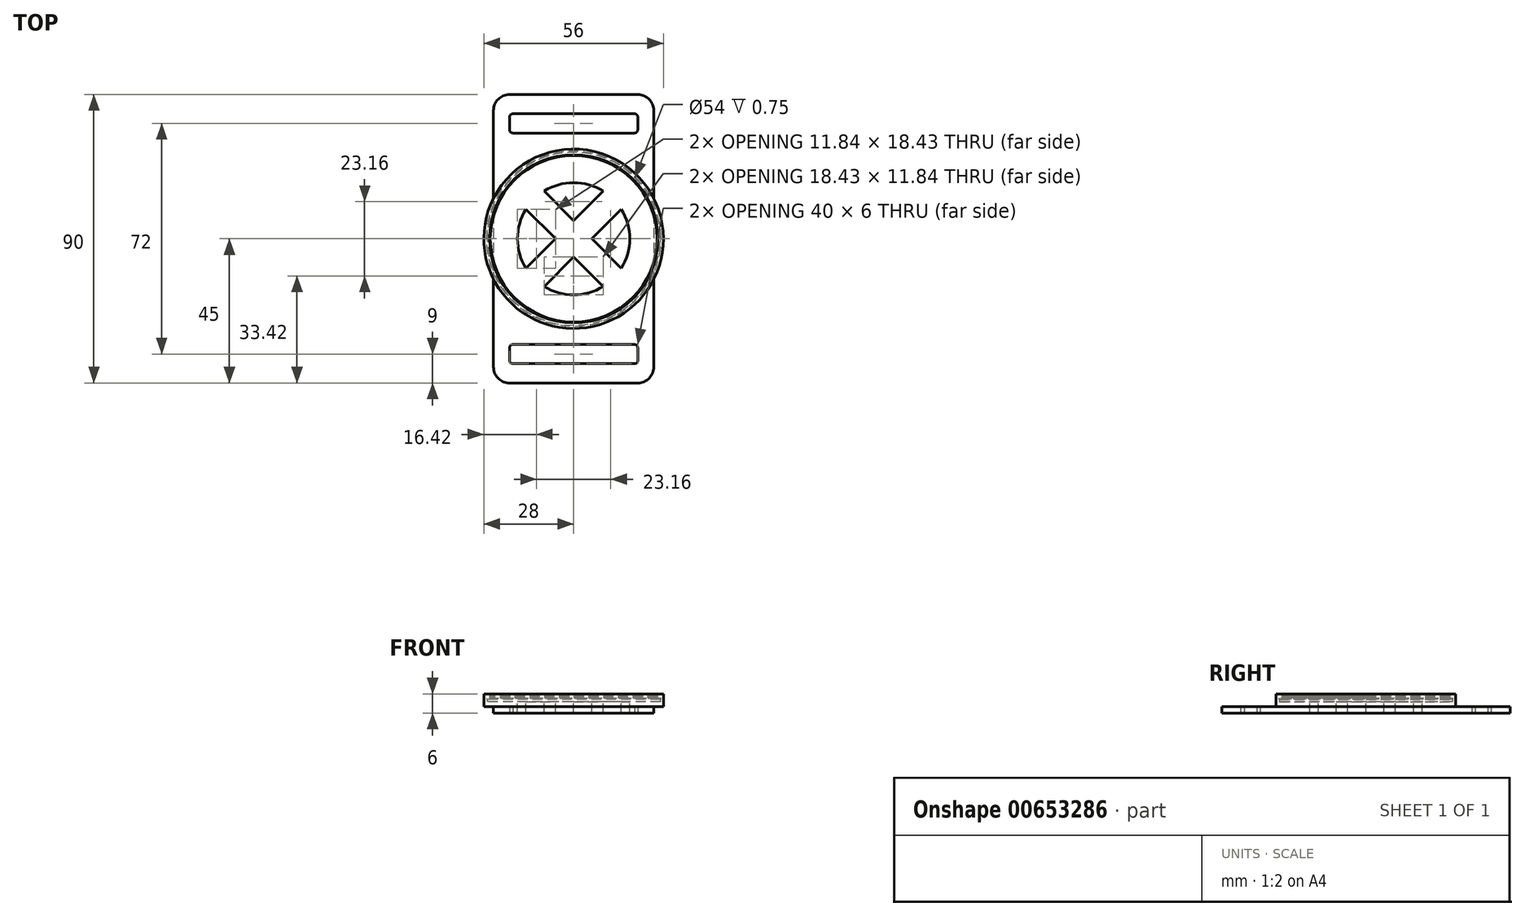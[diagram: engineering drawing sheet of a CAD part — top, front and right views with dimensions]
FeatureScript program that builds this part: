
annotation { "Feature Type Name" : "Feature", "Feature Type Description" : "" }
export const myFeature = defineFeature(function(context is Context, id is Id, definition is map)
    precondition{}
    {
        {
            var Q0;
            Q0=qCreatedBy(makeId("Top.planeOp"),FACE);
            var sketch = newSketch(context, id + "F0", { "sketchPlane" : qUnion([Q0])});
            skLineSegment(sketch, "E0.bottom", {"start": v(-25, 45) * mm, "end": v(25, 45) * mm});
            skLineSegment(sketch, "E0.top", {"start": v(-25, -45) * mm, "end": v(25, -45) * mm});
            skLineSegment(sketch, "E0.left", {"start": v(-25, 45) * mm, "end": v(-25, -45) * mm});
            skLineSegment(sketch, "E0.right", {"start": v(25, 45) * mm, "end": v(25, -45) * mm});
            skLineSegment(sketch, "E1", {"start": v(-25, 0) * mm, "end": v(25, 0) * mm, "construction": true});
            skLineSegment(sketch, "E2", {"start": v(0, -45) * mm, "end": v(0, 45) * mm, "construction": true});
            skPoint(sketch, "E3", {"position": v(0, 0) * mm});
            skSolve(sketch);
        }
        {
            var Q0;
            Q0 = qSketchRegion(id + "F0", true);
            extrude(context, id + "F1", {"entities" : qUnion([Q0]), "depth" : 2 * mm, "offsetDistance" : 25 * mm});
        }
        {
            var Q0;
            Q0=makeQuery(id+"F1.opExtrude","CAP_FACE",FACE,{"disambiguationData":[OSD([sQuery(id+"F0.wireOp",EDGE,"E0.bottom"),sQuery(id+"F0.wireOp",EDGE,"E0.top"),sQuery(id+"F0.wireOp",EDGE,"E0.left"),sQuery(id+"F0.wireOp",EDGE,"E0.right")])],"isStart":false});
            var sketch = newSketch(context, id + "F2", { "sketchPlane" : qUnion([Q0])});
            skCircle(sketch, "E4", {"center": v(0, 0) * mm, "radius": 28 * mm});
            skSolve(sketch);
        }
        {
            var Q0;
            Q0 = qSketchRegion(id + "F2", true);
            extrude(context, id + "F3", {"entities" : qUnion([Q0]), "operationType" : NewBodyOperationType.ADD, "depth" : 1.5 * mm, "offsetDistance" : 25 * mm});
        }
        {
            var Q0;
            Q0=makeQuery(id+"F3.opExtrude","CAP_FACE",FACE,{"disambiguationData":[OSD([sQuery(id+"F2.wireOp",EDGE,"E4")])],"isStart":false});
            var sketch = newSketch(context, id + "F4", { "sketchPlane" : qUnion([Q0])});
            skCircle(sketch, "E5", {"center": v(0, 0) * mm, "radius": 27 * mm});
            skSolve(sketch);
        }
        {
            var Q0;
            Q0=makeQuery(id+"F4.imprint","IMPRINT",FACE,{"disambiguationData":[TD([[makeQuery(id+"F4.imprint","IMPRINT",EDGE,{"derivedFrom":sQuery(id+"F4.wireOp",EDGE,"E5")}),-1.0]])]});
            extrude(context, id + "F5", {"entities" : qUnion([Q0]), "operationType" : NewBodyOperationType.ADD, "depth" : 1 * mm, "offsetDistance" : 25 * mm});
        }
        {
            var Q0;
            Q0=makeQuery(id+"F1.opExtrude","CAP_FACE",FACE,{"disambiguationData":[OSD([sQuery(id+"F0.wireOp",EDGE,"E0.bottom"),sQuery(id+"F0.wireOp",EDGE,"E0.top"),sQuery(id+"F0.wireOp",EDGE,"E0.left"),sQuery(id+"F0.wireOp",EDGE,"E0.right")])],"isStart":true});
            var sketch = newSketch(context, id + "F6", { "sketchPlane" : qUnion([Q0])});
            skLineSegment(sketch, "E6.bottom", {"start": v(-25, 35) * mm, "end": v(-22, 35) * mm});
            skLineSegment(sketch, "E6.top", {"start": v(-25, -35) * mm, "end": v(-22, -35) * mm});
            skLineSegment(sketch, "E6.left", {"start": v(-25, 35) * mm, "end": v(-25, -35) * mm});
            skLineSegment(sketch, "E6.right", {"start": v(-22, 35) * mm, "end": v(-22, -35) * mm});
            skLineSegment(sketch, "E7.bottom", {"start": v(22, 35) * mm, "end": v(25, 35) * mm});
            skLineSegment(sketch, "E7.top", {"start": v(22, -35) * mm, "end": v(25, -35) * mm});
            skLineSegment(sketch, "E7.left", {"start": v(22, 35) * mm, "end": v(22, -35) * mm});
            skLineSegment(sketch, "E7.right", {"start": v(25, 35) * mm, "end": v(25, -35) * mm});
            skSolve(sketch);
        }
        {
            var Q0;
            Q0=makeQuery(id+"F6.imprint","IMPRINT",FACE,{"disambiguationData":[TD([[makeQuery(id+"F6.imprint","IMPRINT",EDGE,{"derivedFrom":sQuery(id+"F6.wireOp",EDGE,"E6.bottom")}),-1.0]])]});
            var Q1;
            Q1=makeQuery(id+"F6.imprint","IMPRINT",FACE,{"disambiguationData":[TD([[makeQuery(id+"F6.imprint","IMPRINT",EDGE,{"derivedFrom":sQuery(id+"F6.wireOp",EDGE,"E7.bottom")}),-1.0]])]});
            extrude(context, id + "F7", {"entities" : qUnion([Q0, Q1]), "operationType" : NewBodyOperationType.ADD, "depth" : 3 * mm, "offsetDistance" : 25 * mm});
        }
        {
            var Q0;
            {var subQ0=sQuery(id+"F6.wireOp",EDGE,"E6.right");var subQ2=sQuery(id+"F6.wireOp",EDGE,"E6.left");var subQ3=sQuery(id+"F6.wireOp",EDGE,"E6.top");Q0=makeQuery(id+"Fcp3DyhTEGZhcjd_1.boolean.opBoolean","SPLIT",FACE,{"disambiguationData":[TD([makeQuery(id+"F7.opExtrude","SWEPT_FACE",FACE,{"disambiguationData":[OSD([subQ3])]})])],"derivedFrom":makeQuery(id+"F7.opExtrude","CAP_FACE",FACE,{"disambiguationData":[OSD([sQuery(id+"F6.wireOp",EDGE,"E6.bottom"),subQ3,subQ2,subQ0])],"isStart":false})});}
            var Q1;
            {var subQ0=sQuery(id+"F6.wireOp",EDGE,"E7.right");var subQ1=sQuery(id+"F6.wireOp",EDGE,"E7.left");var subQ2=sQuery(id+"F6.wireOp",EDGE,"E7.top");Q1=makeQuery(id+"Fcp3DyhTEGZhcjd_1.boolean.opBoolean","SPLIT",FACE,{"disambiguationData":[TD([makeQuery(id+"F7.opExtrude","SWEPT_FACE",FACE,{"disambiguationData":[OSD([subQ2])]})])],"derivedFrom":makeQuery(id+"F7.opExtrude","CAP_FACE",FACE,{"disambiguationData":[OSD([sQuery(id+"F6.wireOp",EDGE,"E7.bottom"),subQ2,subQ1,subQ0])],"isStart":false})});}
            var Q2;
            {var subQ0=sQuery(id+"F6.wireOp",EDGE,"E6.left");var subQ1=sQuery(id+"F6.wireOp",EDGE,"E6.right");var subQ3=sQuery(id+"F6.wireOp",EDGE,"E6.bottom");Q2=makeQuery(id+"Fcp3DyhTEGZhcjd_1.boolean.opBoolean","SPLIT",FACE,{"disambiguationData":[TD([makeQuery(id+"F7.opExtrude","SWEPT_FACE",FACE,{"disambiguationData":[OSD([subQ3])]})])],"derivedFrom":makeQuery(id+"F7.opExtrude","CAP_FACE",FACE,{"disambiguationData":[OSD([subQ3,sQuery(id+"F6.wireOp",EDGE,"E6.top"),subQ0,subQ1])],"isStart":false})});}
            var Q3;
            {var subQ0=sQuery(id+"F6.wireOp",EDGE,"E7.left");var subQ1=sQuery(id+"F6.wireOp",EDGE,"E7.right");var subQ2=sQuery(id+"F6.wireOp",EDGE,"E7.bottom");Q3=makeQuery(id+"Fcp3DyhTEGZhcjd_1.boolean.opBoolean","SPLIT",FACE,{"disambiguationData":[TD([makeQuery(id+"F7.opExtrude","SWEPT_FACE",FACE,{"disambiguationData":[OSD([subQ2])]})])],"derivedFrom":makeQuery(id+"F7.opExtrude","CAP_FACE",FACE,{"disambiguationData":[OSD([subQ2,sQuery(id+"F6.wireOp",EDGE,"E7.top"),subQ0,subQ1])],"isStart":false})});}
            var Q4;
            Q4=makeQuery(id+"F1.opExtrude","CAP_FACE",FACE,{"disambiguationData":[OSD([sQuery(id+"F0.wireOp",EDGE,"E0.bottom"),sQuery(id+"F0.wireOp",EDGE,"E0.top"),sQuery(id+"F0.wireOp",EDGE,"E0.left"),sQuery(id+"F0.wireOp",EDGE,"E0.right")])],"isStart":true});
            extrude(context, id + "F8", {"entities" : qUnion([Q0, Q1, Q2, Q3]), "operationType" : NewBodyOperationType.REMOVE, "endBound" : BoundingType.UP_TO_SURFACE, "oppositeDirection" : true, "depth" : 25 * mm, "endBoundEntityFace" : qUnion([Q4]), "offsetDistance" : 25 * mm});
        }
        {
            var Q0;
            Q0=makeQuery(id+"F3.opExtrude","CAP_FACE",FACE,{"disambiguationData":[OSD([sQuery(id+"F2.wireOp",EDGE,"E4")])],"isStart":false});
            var sketch = newSketch(context, id + "F9", { "sketchPlane" : qUnion([Q0])});
            skCircle(sketch, "E8", {"center": v(0, 0) * mm, "radius": 17.5 * mm});
            skLineSegment(sketch, "E9", {"start": v(14.88, -9.22) * mm, "end": v(5.66, 0) * mm});
            skLineSegment(sketch, "E10", {"start": v(-14.88, 9.22) * mm, "end": v(-5.66, 0) * mm});
            skLineSegment(sketch, "E11", {"start": v(14.88, 9.22) * mm, "end": v(5.66, 0) * mm});
            skLineSegment(sketch, "E12", {"start": v(-14.88, -9.22) * mm, "end": v(-5.66, 0) * mm});
            skLineSegment(sketch, "E13.trimOffspring", {"start": v(0, -5.66) * mm, "end": v(9.22, -14.88) * mm});
            skLineSegment(sketch, "E14.trimOffspring", {"start": v(0, 5.66) * mm, "end": v(9.22, 14.88) * mm});
            skLineSegment(sketch, "E15.trimOffspring", {"start": v(0, 5.66) * mm, "end": v(-9.22, 14.88) * mm});
            skLineSegment(sketch, "E16.trimOffspring", {"start": v(0, -5.66) * mm, "end": v(-9.22, -14.88) * mm});
            skLineSegment(sketch, "E17", {"start": v(0, 5.66) * mm, "end": v(0, 0) * mm, "construction": true});
            skLineSegment(sketch, "E18", {"start": v(-5.66, 0) * mm, "end": v(0, 0) * mm, "construction": true});
            skLineSegment(sketch, "E19", {"start": v(5.66, 0) * mm, "end": v(0, 0) * mm, "construction": true});
            skLineSegment(sketch, "E20", {"start": v(0, 0) * mm, "end": v(0, -5.66) * mm, "construction": true});
            skSolve(sketch);
        }
        {
            var Q0;
            {var subQ0=sQuery(id+"F9.wireOp",EDGE,"E10");Q0=makeQuery(id+"F9.imprint","IMPRINT",FACE,{"disambiguationData":[TD([[makeQuery(id+"F9.imprint","IMPRINT",EDGE,{"derivedFrom":subQ0}),-1.0]])]});}
            var Q1;
            {var subQ0=sQuery(id+"F9.wireOp",EDGE,"E13.trimOffspring");Q1=makeQuery(id+"F9.imprint","IMPRINT",FACE,{"disambiguationData":[TD([[makeQuery(id+"F9.imprint","IMPRINT",EDGE,{"derivedFrom":subQ0}),-1.0]])]});}
            var Q2;
            {var subQ0=sQuery(id+"F9.wireOp",EDGE,"E9");Q2=makeQuery(id+"F9.imprint","IMPRINT",FACE,{"disambiguationData":[TD([[makeQuery(id+"F9.imprint","IMPRINT",EDGE,{"derivedFrom":subQ0}),-1.0]])]});}
            var Q3;
            {var subQ0=sQuery(id+"F9.wireOp",EDGE,"E14.trimOffspring");Q3=makeQuery(id+"F9.imprint","IMPRINT",FACE,{"disambiguationData":[TD([[makeQuery(id+"F9.imprint","IMPRINT",EDGE,{"derivedFrom":subQ0}),1.0]])]});}
            extrude(context, id + "F10", {"entities" : qUnion([Q0, Q1, Q2, Q3]), "operationType" : NewBodyOperationType.REMOVE, "oppositeDirection" : true, "depth" : 25 * mm, "offsetDistance" : 25 * mm});
        }
        {
            var Q0;
            {var subQ0=sQuery(id+"F0.wireOp",EDGE,"E0.right");var subQ1=sQuery(id+"F0.wireOp",EDGE,"E0.left");var subQ2=sQuery(id+"F0.wireOp",EDGE,"E0.top");var subQ3=sQuery(id+"F0.wireOp",EDGE,"E0.bottom");Q0=makeQuery(id+"F8.boolean.opBoolean","MERGE",FACE,{"derivedFrom":[makeQuery(id+"F1.opExtrude","CAP_FACE",FACE,{"disambiguationData":[OSD([subQ3,subQ2,subQ1,subQ0])],"isStart":true}),makeQuery(id+"F8.opExtrude","CAP_FACE",FACE,{"disambiguationData":[OSD([subQ3,subQ2,subQ1,subQ0]),OD(0.0)],"isStart":false}),makeQuery(id+"F8.opExtrude","CAP_FACE",FACE,{"disambiguationData":[OSD([subQ3,subQ2,subQ1,subQ0]),OD(1.0)],"isStart":false}),makeQuery(id+"F8.opExtrude","CAP_FACE",FACE,{"disambiguationData":[OSD([subQ3,subQ2,subQ1,subQ0]),OD(2.0)],"isStart":false}),makeQuery(id+"F8.opExtrude","CAP_FACE",FACE,{"disambiguationData":[OSD([subQ3,subQ2,subQ1,subQ0]),OD(3.0)],"isStart":false})]});}
            var sketch = newSketch(context, id + "F11", { "sketchPlane" : qUnion([Q0])});
            skLineSegment(sketch, "E21.bottom", {"start": v(19, 39) * mm, "end": v(-19, 39) * mm});
            skLineSegment(sketch, "E21.top", {"start": v(19, 33) * mm, "end": v(-19, 33) * mm});
            skLineSegment(sketch, "E21.left", {"start": v(20, 38) * mm, "end": v(20, 34) * mm});
            skLineSegment(sketch, "E21.right", {"start": v(-20, 38) * mm, "end": v(-20, 34) * mm});
            skLineSegment(sketch, "E22.bottom", {"start": v(19, -33) * mm, "end": v(-19, -33) * mm});
            skLineSegment(sketch, "E22.top", {"start": v(19, -39) * mm, "end": v(-19, -39) * mm});
            skLineSegment(sketch, "E22.left", {"start": v(20, -34) * mm, "end": v(20, -38) * mm});
            skLineSegment(sketch, "E22.right", {"start": v(-20, -34) * mm, "end": v(-20, -38) * mm});
            skPoint(sketch, "E23.visualSharp", {"position": v(20, 39) * mm});
            skArc(sketch, "E23.filletArc", {"start": v(20, 38) * mm, "mid": v(19.7, 38.7) * mm, "end": v(19, 39) * mm});
            skPoint(sketch, "E24.visualSharp", {"position": v(20, 33) * mm});
            skArc(sketch, "E24.filletArc", {"start": v(19, 33) * mm, "mid": v(19.7, 33.3) * mm, "end": v(20, 34) * mm});
            skPoint(sketch, "E25.visualSharp", {"position": v(-20, 33) * mm});
            skArc(sketch, "E25.filletArc", {"start": v(-20, 34) * mm, "mid": v(-19.7, 33.3) * mm, "end": v(-19, 33) * mm});
            skPoint(sketch, "E26.visualSharp", {"position": v(-20, 39) * mm});
            skArc(sketch, "E26.filletArc", {"start": v(-19, 39) * mm, "mid": v(-19.7, 38.7) * mm, "end": v(-20, 38) * mm});
            skPoint(sketch, "E27.visualSharp", {"position": v(-20, -33) * mm});
            skArc(sketch, "E27.filletArc", {"start": v(-19, -33) * mm, "mid": v(-19.7, -33.3) * mm, "end": v(-20, -34) * mm});
            skPoint(sketch, "E28.visualSharp", {"position": v(-20, -39) * mm});
            skArc(sketch, "E28.filletArc", {"start": v(-20, -38) * mm, "mid": v(-19.7, -38.7) * mm, "end": v(-19, -39) * mm});
            skPoint(sketch, "E29.visualSharp", {"position": v(20, -39) * mm});
            skArc(sketch, "E29.filletArc", {"start": v(19, -39) * mm, "mid": v(19.7, -38.7) * mm, "end": v(20, -38) * mm});
            skPoint(sketch, "E30.visualSharp", {"position": v(20, -33) * mm});
            skArc(sketch, "E30.filletArc", {"start": v(20, -34) * mm, "mid": v(19.7, -33.3) * mm, "end": v(19, -33) * mm});
            skLineSegment(sketch, "E31.bottom", {"start": v(-4, 39) * mm, "end": v(4, 39) * mm});
            skLineSegment(sketch, "E31.top", {"start": v(-4, 45) * mm, "end": v(4, 45) * mm});
            skLineSegment(sketch, "E31.left", {"start": v(-4, 39) * mm, "end": v(-4, 45) * mm});
            skLineSegment(sketch, "E31.right", {"start": v(4, 39) * mm, "end": v(4, 45) * mm});
            skLineSegment(sketch, "E32.bottom", {"start": v(4, -39) * mm, "end": v(-4, -39) * mm});
            skLineSegment(sketch, "E32.top", {"start": v(4, -45) * mm, "end": v(-4, -45) * mm});
            skLineSegment(sketch, "E32.left", {"start": v(4, -39) * mm, "end": v(4, -45) * mm});
            skLineSegment(sketch, "E32.right", {"start": v(-4, -39) * mm, "end": v(-4, -45) * mm});
            skSolve(sketch);
        }
        {
            var Q0;
            Q0=makeQuery(id+"F11.imprint","IMPRINT",FACE,{"disambiguationData":[TD([[makeQuery(id+"F11.imprint","IMPRINT",EDGE,{"derivedFrom":sQuery(id+"F11.wireOp",EDGE,"E32.bottom")}),1.0]])]});
            var Q1;
            Q1=makeQuery(id+"F11.imprint","IMPRINT",FACE,{"disambiguationData":[TD([[makeQuery(id+"F11.imprint","IMPRINT",EDGE,{"derivedFrom":sQuery(id+"F11.wireOp",EDGE,"E22.bottom")}),1.0]])]});
            var Q2;
            Q2=makeQuery(id+"F11.imprint","IMPRINT",FACE,{"disambiguationData":[TD([[makeQuery(id+"F11.imprint","IMPRINT",EDGE,{"derivedFrom":sQuery(id+"F11.wireOp",EDGE,"E31.bottom")}),1.0]])]});
            var Q3;
            Q3=makeQuery(id+"F11.imprint","IMPRINT",FACE,{"disambiguationData":[TD([[makeQuery(id+"F11.imprint","IMPRINT",EDGE,{"derivedFrom":sQuery(id+"F11.wireOp",EDGE,"E21.top")}),-1.0]])]});
            extrude(context, id + "F12", {"entities" : qUnion([Q0, Q1, Q2, Q3]), "operationType" : NewBodyOperationType.REMOVE, "oppositeDirection" : true, "depth" : 25 * mm, "offsetDistance" : 25 * mm});
        }
        {
            var Q0;
            Q0=makeQuery(id+"F12.boolean.opBoolean","COPY",EDGE,{"derivedFrom":makeQuery(id+"F12.opExtrude","SWEPT_EDGE",EDGE,{"disambiguationData":[OSD([sQuery(id+"F0.wireOp",EDGE,"E0.top"),sQuery(id+"F11.wireOp",EDGE,"E31.top"),sQuery(id+"F11.wireOp",EDGE,"E31.left")])]})});
            var Q1;
            Q1=makeQuery(id+"F12.boolean.opBoolean","COPY",EDGE,{"derivedFrom":makeQuery(id+"F12.opExtrude","SWEPT_EDGE",EDGE,{"disambiguationData":[OSD([sQuery(id+"F11.wireOp",EDGE,"E21.bottom"),sQuery(id+"F11.wireOp",EDGE,"E31.bottom"),sQuery(id+"F11.wireOp",EDGE,"E31.left")])]})});
            var Q2;
            Q2=makeQuery(id+"F12.boolean.opBoolean","COPY",EDGE,{"derivedFrom":makeQuery(id+"F12.opExtrude","SWEPT_EDGE",EDGE,{"disambiguationData":[OSD([sQuery(id+"F0.wireOp",EDGE,"E0.top"),sQuery(id+"F11.wireOp",EDGE,"E31.top"),sQuery(id+"F11.wireOp",EDGE,"E31.right")])]})});
            var Q3;
            Q3=makeQuery(id+"F12.boolean.opBoolean","COPY",EDGE,{"derivedFrom":makeQuery(id+"F12.opExtrude","SWEPT_EDGE",EDGE,{"disambiguationData":[OSD([sQuery(id+"F11.wireOp",EDGE,"E21.bottom"),sQuery(id+"F11.wireOp",EDGE,"E31.bottom"),sQuery(id+"F11.wireOp",EDGE,"E31.right")])]})});
            fillet(context, id + "F13", {"entities" : qUnion([Q0, Q1, Q2, Q3]), "radius" : 1 * mm, "tangentPropagation" : true, "allowEdgeOverflow" : false});
        }
        {
            var Q0;
            Q0=makeQuery(id+"F12.boolean.opBoolean","COPY",EDGE,{"derivedFrom":makeQuery(id+"F12.opExtrude","SWEPT_EDGE",EDGE,{"disambiguationData":[OSD([sQuery(id+"F0.wireOp",EDGE,"E0.bottom"),sQuery(id+"F11.wireOp",EDGE,"E32.top"),sQuery(id+"F11.wireOp",EDGE,"E32.left")])]})});
            var Q1;
            Q1=makeQuery(id+"F12.boolean.opBoolean","COPY",EDGE,{"derivedFrom":makeQuery(id+"F12.opExtrude","SWEPT_EDGE",EDGE,{"disambiguationData":[OSD([sQuery(id+"F11.wireOp",EDGE,"E22.top"),sQuery(id+"F11.wireOp",EDGE,"E32.bottom"),sQuery(id+"F11.wireOp",EDGE,"E32.left")])]})});
            var Q2;
            Q2=makeQuery(id+"F12.boolean.opBoolean","COPY",EDGE,{"derivedFrom":makeQuery(id+"F12.opExtrude","SWEPT_EDGE",EDGE,{"disambiguationData":[OSD([sQuery(id+"F0.wireOp",EDGE,"E0.bottom"),sQuery(id+"F11.wireOp",EDGE,"E32.top"),sQuery(id+"F11.wireOp",EDGE,"E32.right")])]})});
            var Q3;
            Q3=makeQuery(id+"F12.boolean.opBoolean","COPY",EDGE,{"derivedFrom":makeQuery(id+"F12.opExtrude","SWEPT_EDGE",EDGE,{"disambiguationData":[OSD([sQuery(id+"F11.wireOp",EDGE,"E22.top"),sQuery(id+"F11.wireOp",EDGE,"E32.bottom"),sQuery(id+"F11.wireOp",EDGE,"E32.right")])]})});
            fillet(context, id + "F14", {"entities" : qUnion([Q0, Q1, Q2, Q3]), "radius" : 1 * mm, "tangentPropagation" : true, "allowEdgeOverflow" : false});
        }
        {
            var Q0;
            Q0=makeQuery(id+"F1.opExtrude","SWEPT_EDGE",EDGE,{"disambiguationData":[OSD([sQuery(id+"F0.wireOp",EDGE,"E0.top"),sQuery(id+"F0.wireOp",EDGE,"E0.right")])]});
            var Q1;
            Q1=makeQuery(id+"F1.opExtrude","SWEPT_EDGE",EDGE,{"disambiguationData":[OSD([sQuery(id+"F0.wireOp",EDGE,"E0.bottom"),sQuery(id+"F0.wireOp",EDGE,"E0.right")])]});
            var Q2;
            Q2=makeQuery(id+"F1.opExtrude","SWEPT_EDGE",EDGE,{"disambiguationData":[OSD([sQuery(id+"F0.wireOp",EDGE,"E0.bottom"),sQuery(id+"F0.wireOp",EDGE,"E0.left")])]});
            var Q3;
            Q3=makeQuery(id+"F1.opExtrude","SWEPT_EDGE",EDGE,{"disambiguationData":[OSD([sQuery(id+"F0.wireOp",EDGE,"E0.top"),sQuery(id+"F0.wireOp",EDGE,"E0.left")])]});
            fillet(context, id + "F15", {"entities" : qUnion([Q0, Q1, Q2, Q3]), "radius" : 5 * mm, "tangentPropagation" : true, "allowEdgeOverflow" : false});
        }
        {
            var Q0;
            Q0=makeQuery(id+"F1.opExtrude","SWEPT_BODY",BODY,{"disambiguationData":[OSD([sQuery(id+"F0.wireOp",EDGE,"E0.bottom"),sQuery(id+"F0.wireOp",EDGE,"E0.top"),sQuery(id+"F0.wireOp",EDGE,"E0.left"),sQuery(id+"F0.wireOp",EDGE,"E0.right")])]});
            transform(context, id + "F16", {"entities" : qUnion([Q0]), "transformType" : TransformType.TRANSLATION_3D, "dx" : 72.1 * mm, "dy" : 0 * mm, "dz" : 0 * mm, "makeCopy" : true});
        }
        {
            var Q0;
            Q0=makeQuery(id+"F16.opPattern","COPY",BODY,{"derivedFrom":makeQuery(id+"F1.opExtrude","SWEPT_BODY",BODY,{"disambiguationData":[OSD([sQuery(id+"F0.wireOp",EDGE,"E0.bottom"),sQuery(id+"F0.wireOp",EDGE,"E0.top"),sQuery(id+"F0.wireOp",EDGE,"E0.left"),sQuery(id+"F0.wireOp",EDGE,"E0.right")])]}),"instanceName":"1"});
            deleteBodies(context, id + "F17", {"entities" : qUnion([Q0])});
        }
        {
            var Q0;
            Q0=makeQuery(id+"F5.opExtrude","CAP_EDGE",EDGE,{"disambiguationData":[OSD([sQuery(id+"F4.wireOp",EDGE,"E5")])],"isStart":false});
            chamfer(context, id + "F18", {"entities" : qUnion([Q0]), "width" : 0.25 * mm, "tangentPropagation" : true});
        }
        {
            var Q0;
            Q0=makeQuery(id+"F5.opExtrude","CAP_FACE",FACE,{"disambiguationData":[OSD([sQuery(id+"F2.wireOp",EDGE,"E4"),sQuery(id+"F4.wireOp",EDGE,"E5")])],"isStart":false});
            var sketch = newSketch(context, id + "F19", { "sketchPlane" : qUnion([Q0])});
            skCircle(sketch, "E33", {"center": v(0, 0) * mm, "radius": 26 * mm});
            skSolve(sketch);
        }
        {
            var Q0;
            Q0=makeQuery(id+"F19.imprint","IMPRINT",FACE,{"disambiguationData":[TD([[makeQuery(id+"F19.imprint","IMPRINT",EDGE,{"derivedFrom":sQuery(id+"F19.wireOp",EDGE,"E33")}),-1.0]])]});
            var Q1;
            {var subQ0=sQuery(id+"F2.wireOp",EDGE,"E4");Q1=makeQuery(id+"F19.imprint","IMPRINT",FACE,{"disambiguationData":[TD([[makeQuery(id+"F19.imprint","IMPRINT",EDGE,{"derivedFrom":makeQuery(id+"F5.opExtrude","CAP_EDGE",EDGE,{"disambiguationData":[OSD([subQ0])],"isStart":false})}),1.0]])]});}
            extrude(context, id + "F20", {"entities" : qUnion([Q0, Q1]), "operationType" : NewBodyOperationType.ADD, "depth" : 0.5 * mm, "offsetDistance" : 25 * mm});
        }
        {
            var Q0;
            Q0=makeQuery(id+"F20.opExtrude","CAP_EDGE",EDGE,{"disambiguationData":[OSD([sQuery(id+"F19.wireOp",EDGE,"E33")])],"isStart":true});
            var Q1;
            Q1=makeQuery(id+"F20.opExtrude","CAP_EDGE",EDGE,{"disambiguationData":[OSD([sQuery(id+"F19.wireOp",EDGE,"E33")])],"isStart":false});
            chamfer(context, id + "F21", {"entities" : qUnion([Q0, Q1]), "width" : 0.25 * mm, "tangentPropagation" : true});
        }
        {
            var Q0;
            Q0=makeQuery(id+"F20.opExtrude","CAP_FACE",FACE,{"disambiguationData":[OSD([sQuery(id+"F2.wireOp",EDGE,"E4"),sQuery(id+"F19.wireOp",EDGE,"E33")])],"isStart":false});
            var sketch = newSketch(context, id + "F22", { "sketchPlane" : qUnion([Q0])});
            skCircle(sketch, "E34", {"center": v(0, 0) * mm, "radius": 26 * mm});
            skSolve(sketch);
        }
        {
            var Q0;
            Q0=makeQuery(id+"F22.imprint","IMPRINT",FACE,{"disambiguationData":[TD([[makeQuery(id+"F22.imprint","IMPRINT",EDGE,{"derivedFrom":sQuery(id+"F22.wireOp",EDGE,"E34")}),-1.0]])]});
            var Q1;
            {var subQ0=sQuery(id+"F2.wireOp",EDGE,"E4");Q1=makeQuery(id+"F22.imprint","IMPRINT",FACE,{"disambiguationData":[TD([[makeQuery(id+"F22.imprint","IMPRINT",EDGE,{"derivedFrom":makeQuery(id+"F20.opExtrude","CAP_EDGE",EDGE,{"disambiguationData":[OSD([subQ0])],"isStart":false})}),1.0]])]});}
            extrude(context, id + "F23", {"entities" : qUnion([Q0, Q1]), "operationType" : NewBodyOperationType.ADD, "depth" : 0.5 * mm, "offsetDistance" : 25 * mm});
        }
        {
            var Q0;
            Q0=makeQuery(id+"F23.opExtrude","CAP_EDGE",EDGE,{"disambiguationData":[OSD([sQuery(id+"F22.wireOp",EDGE,"E34")])],"isStart":true});
            var Q1;
            Q1=makeQuery(id+"F23.opExtrude","CAP_EDGE",EDGE,{"disambiguationData":[OSD([sQuery(id+"F22.wireOp",EDGE,"E34")])],"isStart":false});
            chamfer(context, id + "F24", {"entities" : qUnion([Q0, Q1]), "width" : 0.25 * mm, "tangentPropagation" : true});
        }
        {
            var Q0;
            Q0=makeQuery(id+"F23.opExtrude","CAP_FACE",FACE,{"disambiguationData":[OSD([sQuery(id+"F2.wireOp",EDGE,"E4"),sQuery(id+"F22.wireOp",EDGE,"E34")])],"isStart":false});
            var sketch = newSketch(context, id + "F25", { "sketchPlane" : qUnion([Q0])});
            skCircle(sketch, "E35", {"center": v(0, 0) * mm, "radius": 26 * mm});
            skSolve(sketch);
        }
        {
            var Q0;
            Q0=makeQuery(id+"F25.imprint","IMPRINT",FACE,{"disambiguationData":[TD([[makeQuery(id+"F25.imprint","IMPRINT",EDGE,{"derivedFrom":sQuery(id+"F25.wireOp",EDGE,"E35")}),-1.0]])]});
            var Q1;
            {var subQ0=sQuery(id+"F2.wireOp",EDGE,"E4");Q1=makeQuery(id+"F25.imprint","IMPRINT",FACE,{"disambiguationData":[TD([[makeQuery(id+"F25.imprint","IMPRINT",EDGE,{"derivedFrom":makeQuery(id+"F23.opExtrude","CAP_EDGE",EDGE,{"disambiguationData":[OSD([subQ0])],"isStart":false})}),1.0]])]});}
            extrude(context, id + "F26", {"entities" : qUnion([Q0, Q1]), "operationType" : NewBodyOperationType.ADD, "depth" : 0.5 * mm, "offsetDistance" : 25 * mm});
        }
        {
            var Q0;
            Q0=makeQuery(id+"F26.opExtrude","CAP_EDGE",EDGE,{"disambiguationData":[OSD([sQuery(id+"F25.wireOp",EDGE,"E35")])],"isStart":false});
            var Q1;
            Q1=makeQuery(id+"F26.opExtrude","CAP_EDGE",EDGE,{"disambiguationData":[OSD([sQuery(id+"F25.wireOp",EDGE,"E35")])],"isStart":true});
            chamfer(context, id + "F27", {"entities" : qUnion([Q0, Q1]), "width" : 0.25 * mm, "tangentPropagation" : true});
        }
    });
